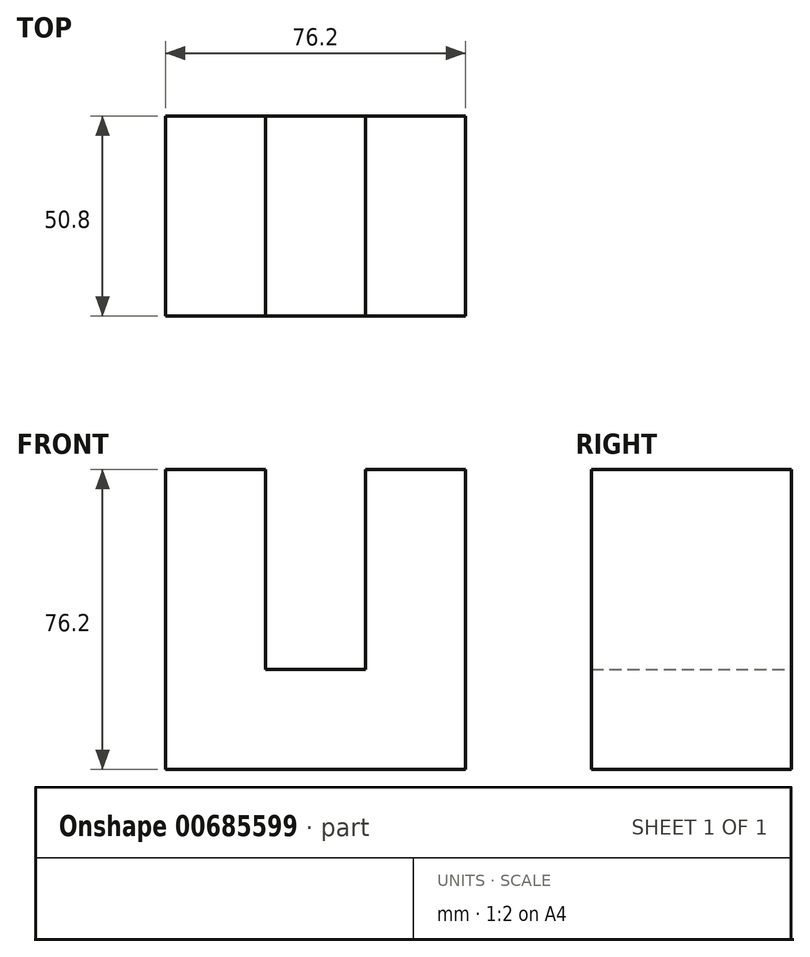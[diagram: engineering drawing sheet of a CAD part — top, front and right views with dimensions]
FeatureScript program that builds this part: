
annotation { "Feature Type Name" : "Feature", "Feature Type Description" : "" }
export const myFeature = defineFeature(function(context is Context, id is Id, definition is map)
    precondition{}
    {
        {
            var Q0;
            Q0=qCreatedBy(makeId("Front.planeOp"),FACE);
            var sketch = newSketch(context, id + "F0", { "sketchPlane" : qUnion([Q0])});
            skLineSegment(sketch, "E0", {"start": v(0, 76.2) * mm, "end": v(0, 0) * mm});
            skLineSegment(sketch, "E1", {"start": v(0, 0) * mm, "end": v(76.2, 0) * mm});
            skLineSegment(sketch, "E2", {"start": v(76.2, 0) * mm, "end": v(76.2, 76.2) * mm});
            skLineSegment(sketch, "E3", {"start": v(76.2, 76.2) * mm, "end": v(50.8, 76.2) * mm});
            skLineSegment(sketch, "E4", {"start": v(50.8, 76.2) * mm, "end": v(50.8, 25.4) * mm});
            skLineSegment(sketch, "E5", {"start": v(50.8, 25.4) * mm, "end": v(25.4, 25.4) * mm});
            skLineSegment(sketch, "E6", {"start": v(25.4, 25.4) * mm, "end": v(25.4, 76.2) * mm});
            skLineSegment(sketch, "E7", {"start": v(25.4, 76.2) * mm, "end": v(0, 76.2) * mm});
            skSolve(sketch);
        }
        {
            var Q0;
            Q0 = qSketchRegion(id + "F0", true);
            extrude(context, id + "F1", {"entities" : qUnion([Q0]), "depth" : 50.8 * mm, "offsetDistance" : 25.4 * mm});
        }
    });
